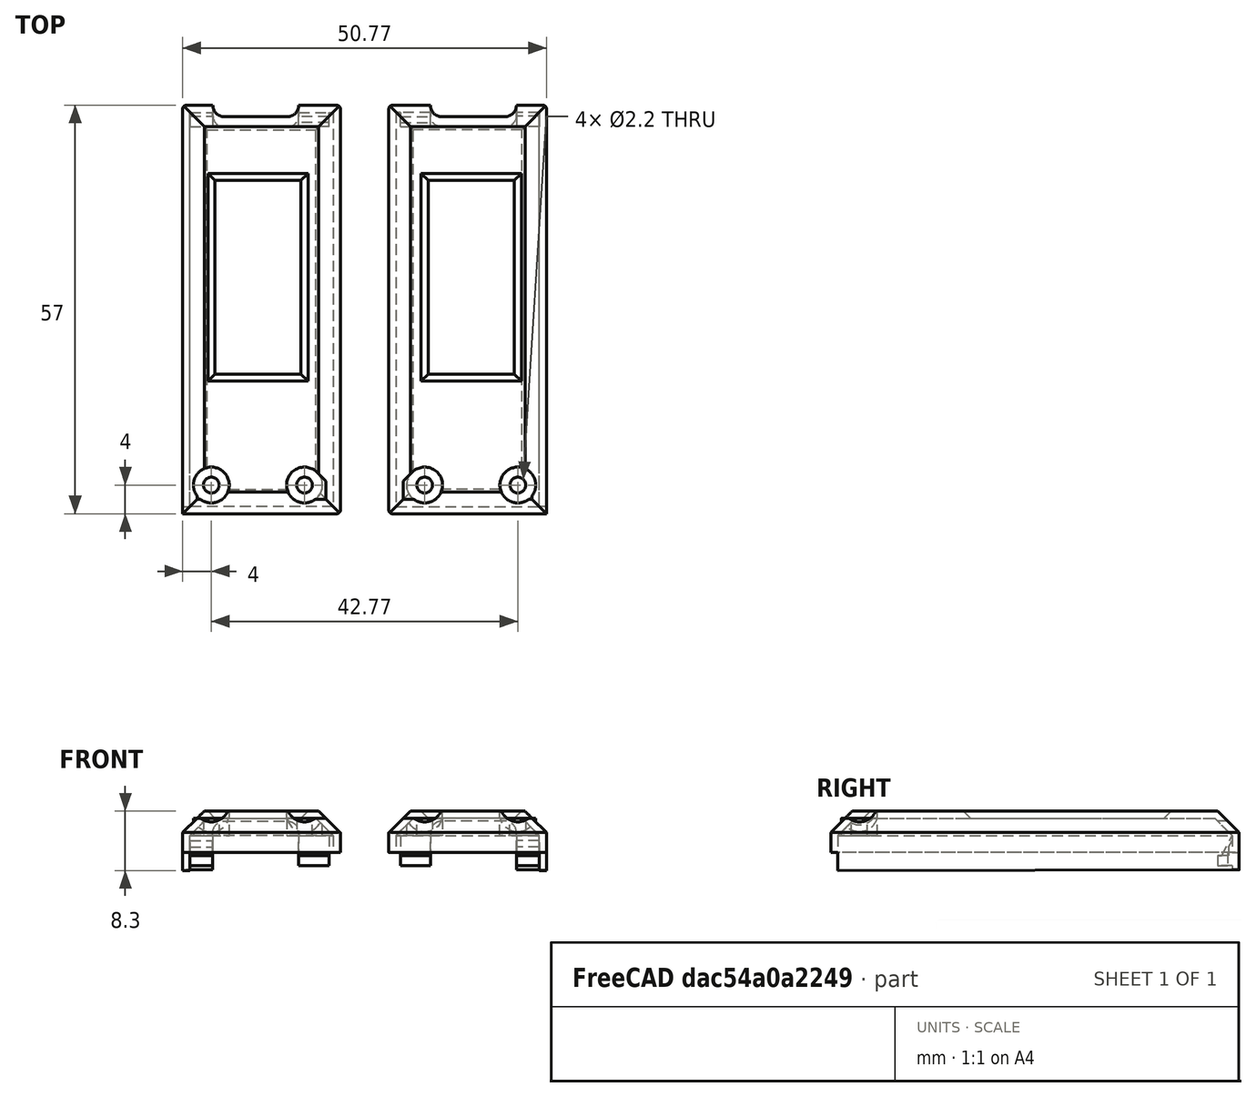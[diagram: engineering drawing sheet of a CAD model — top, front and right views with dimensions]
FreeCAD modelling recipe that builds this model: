
FCSTD DOCUMENT  (FreeCAD 1.0R39285 (Git))
Label: cinque-1.0-cover-Nice
License: All rights reserved
LicenseURL: https://en.wikipedia.org/wiki/All_rights_reserved
objects: Sketcher::SketchObject×13, PartDesign::Pad×6, PartDesign::Pocket×5, PartDesign::Body×2, PartDesign::Chamfer×2, PartDesign::Thickness×1, PartDesign::Fillet×1, Part::Mirroring×1
note: 74 computed .brp shape members not serialized (recipe doc carries the construction recipe); baked Part::Feature solids carry a one-line shape summary decoded from their .brp

FEATURE [PartDesign::Body] Body
  AllowCompound = false
  Origin = -> Origin
FEATURE [Sketcher::SketchObject] Sketch
  ArcFitTolerance = 1e-06
  AttachmentSupport = -> [XY_Plane001]
  FullyConstrained = true
  MakeInternals = false
  MapMode = 5
  sketch-geometry (5):
    g0: LineSegment StartX=-11 StartY=-28.5 StartZ=0 EndX=11 EndY=-28.5 EndZ=0
    g1: LineSegment StartX=11 StartY=-28.5 StartZ=0 EndX=11 EndY=28.5 EndZ=0
    g2: LineSegment StartX=11 StartY=28.5 StartZ=0 EndX=-11 EndY=28.5 EndZ=0
    g3: LineSegment StartX=-11 StartY=28.5 StartZ=0 EndX=-11 EndY=-28.5 EndZ=0
    g4: GeomPoint [constr] X=0 Y=0 Z=0
  constraints (12):
    c: Coincident(g0,g1)
    c: Coincident(g1,g2)
    c: Coincident(g2,g3)
    c: Coincident(g3,g0)
    c: Horizontal(g0)
    c: Horizontal(g2)
    c: Vertical(g1)
    c: Vertical(g3)
    c: Symmetric(g2,g0,g4)
    c: Distance(g1,g3) = 22
    c: Distance(g0,g2) = 57
    c: Coincident(g4,g-1)
FEATURE [PartDesign::Pad] Pad
  Direction = (0,0,1)
  Length = 5.8
  Length2 = 10
  Profile = -> Sketch
  ReferenceAxis = -> Sketch [N_Axis]
  Refine = true
  Suppressed = false
  Type = 0
FEATURE [PartDesign::Chamfer] Chamfer
  Angle = 45
  Base = -> Pad [Face6]
  BaseFeature = -> Pad
  ChamferType = 0
  FlipDirection = false
  Refine = true
  Size = 3
  Size2 = 1
  SupportTransform = false
  Suppressed = false
  UseAllEdges = false
FEATURE [PartDesign::Thickness] Thickness
  Base = -> Chamfer [Face4]
  BaseFeature = -> Chamfer
  Intersection = false
  Join = 0
  Mode = 0
  Refine = true
  Reversed = true
  SupportTransform = false
  Suppressed = false
  Value = 1
FEATURE [Sketcher::SketchObject] Sketch001
  ArcFitTolerance = 1e-06
  AttachmentSupport = -> [Thickness]
  ExternalGeometry = -> [Thickness]
  FullyConstrained = true
  MakeInternals = false
  MapMode = 5
  Placement = pos=(-11,0,0) rot=(0.57735,-0.57735,-0.57735;2.0944rad)
  sketch-geometry (1):
    g0: Circle CenterX=18.5 CenterY=0.2 CenterZ=0 NormalX=0 NormalY=0 NormalZ=1 AngleXU=0 Radius=4.15
  constraints (3):
    c: Diameter(g0) = 8.3
    c: Distance(g0,g-3) = 47
    c: Distance(g0,g-1) = 0.2
FEATURE [Sketcher::SketchObject] Sketch002
  ArcFitTolerance = 1e-06
  AttachmentSupport = -> [Chamfer]
  ExternalGeometry = -> [Chamfer]
  FullyConstrained = true
  MakeInternals = false
  MapMode = 5
  Placement = pos=(0,28.5,0) rot=(0,0.707107,0.707107;3.14159rad)
  sketch-geometry (14):
    g0: LineSegment StartX=-6.8 StartY=-1 StartZ=0 EndX=-6.8 EndY=2.8 EndZ=0
    g1: LineSegment StartX=-5.2 StartY=4.4 StartZ=0 EndX=3.6 EndY=4.4 EndZ=0
    g2: LineSegment StartX=5.2 StartY=2.8 StartZ=0 EndX=5.2 EndY=-1 EndZ=0
    g3: LineSegment StartX=3.6 StartY=-2.6 StartZ=0 EndX=-5.2 EndY=-2.6 EndZ=0
    g4: ArcOfCircle CenterX=-5.2 CenterY=2.8 CenterZ=0 NormalX=0 NormalY=0 NormalZ=1 AngleXU=0 Radius=1.6 StartAngle=1.5708 EndAngle=3.14159
    g5: GeomPoint [constr] X=-6.8 Y=4.4 Z=0
    g6: ArcOfCircle CenterX=3.6 CenterY=2.8 CenterZ=0 NormalX=0 NormalY=0 NormalZ=1 AngleXU=0 Radius=1.6 StartAngle=0 EndAngle=1.5708
    g7: GeomPoint [constr] X=5.2 Y=4.4 Z=0
    g8: ArcOfCircle CenterX=3.6 CenterY=-1 CenterZ=0 NormalX=0 NormalY=0 NormalZ=1 AngleXU=0 Radius=1.6 StartAngle=4.71239 EndAngle=6.28319
    g9: GeomPoint [constr] X=5.2 Y=-2.6 Z=0
    g10: ArcOfCircle CenterX=-5.2 CenterY=-1 CenterZ=0 NormalX=0 NormalY=0 NormalZ=1 AngleXU=0 Radius=1.6 StartAngle=3.14159 EndAngle=4.71239
    g11: GeomPoint [constr] X=-6.8 Y=-2.6 Z=0
    g12: GeomPoint [constr] X=-0.8 Y=4.4 Z=0
    g13: GeomPoint [constr] X=5.2 Y=0.9 Z=0
  constraints (30):
    c: Horizontal(g1)
    c: Parallel(g1,g3)
    c: Parallel(g0,g2)
    c: PointOnObject(g5,g0)
    c: PointOnObject(g5,g1)
    c: Tangent(g0,g4) = 1.5708
    c: Tangent(g1,g4) = 1.5708
    c: PointOnObject(g7,g1)
    c: PointOnObject(g7,g2)
    c: Tangent(g1,g6) = 1.5708
    c: Tangent(g2,g6) = 1.5708
    c: PointOnObject(g9,g2)
    c: PointOnObject(g9,g3)
    c: Tangent(g2,g8) = 1.5708
    c: Tangent(g3,g8) = 1.5708
    c: PointOnObject(g11,g0)
    c: PointOnObject(g11,g3)
    c: Tangent(g0,g10) = 1.5708
    c: Tangent(g3,g10) = 1.5708
    c: Perpendicular(g3,g0)
    c: Symmetric(g1,g1,g12)
    c: Symmetric(g2,g2,g13)
    c: Distance(g13,g-1) = 0.9
    c: Distance(g2,g0) = 12
    c: Distance(g3,g1) = 7
    c: Radius(g10) = 1.6
    c: Radius(g4) = 1.6
    c: Radius(g6) = 1.6
    c: Radius(g8) = 1.6
    c: DistanceX(g12,g-3) = 11.8
FEATURE [PartDesign::Pocket] Pocket001
  BaseFeature = -> Thickness
  Direction = (0,-1,2e-16)
  Length = 5
  Length2 = 5
  Profile = -> Sketch002
  ReferenceAxis = -> Sketch002 [N_Axis]
  Refine = true
  Suppressed = false
  Type = 0
FEATURE [Sketcher::SketchObject] Sketch003
  ArcFitTolerance = 1e-06
  AttachmentOffset = pos=(0,0,4.8) rot=(0,0,1;0rad)
  AttachmentSupport = -> [XY_Plane001]
  ExternalGeometry = -> [Pocket001]
  FullyConstrained = true
  MakeInternals = false
  MapMode = 5
  Placement = pos=(0,0,4.8) rot=(0,0,1;0rad)
  sketch-geometry (3):
    g0: LineSegment [constr] StartX=-11 StartY=-24.5 StartZ=0 EndX=11 EndY=-24.5 EndZ=0
    g1: Circle CenterX=-6 CenterY=-24.5 CenterZ=0 NormalX=0 NormalY=0 NormalZ=1 AngleXU=0 Radius=2.5
    g2: Circle CenterX=7 CenterY=-24.5 CenterZ=0 NormalX=0 NormalY=0 NormalZ=1 AngleXU=0 Radius=2.5
  constraints (10):
    c: PointOnObject(g0,g-4)
    c: Horizontal(g0)
    c: Distance(g0,g-3) = 53
    c: Diameter(g1) = 5
    c: PointOnObject(g1,g0)
    c: Distance(g0,g1) = 5
    c: Diameter(g2) = 5
    c: PointOnObject(g2,g0)
    c: DistanceX(g0,g2) = 18
    c: PointOnObject(g0,g-5)
FEATURE [Sketcher::SketchObject] Sketch004
  ArcFitTolerance = 1e-06
  AttachmentOffset = pos=(0,0,5.8) rot=(0,0,1;0rad)
  AttachmentSupport = -> [XY_Plane001]
  ExternalGeometry = -> [Pocket001]
  FullyConstrained = true
  MakeInternals = false
  MapMode = 5
  Placement = pos=(0,0,5.8) rot=(0,0,1;0rad)
  sketch-geometry (8):
    g0: LineSegment [constr] StartX=-11 StartY=-24.5 StartZ=0 EndX=11 EndY=-24.5 EndZ=0
    g1: ArcOfCircle CenterX=-6 CenterY=-24.5 CenterZ=0 NormalX=0 NormalY=0 NormalZ=1 AngleXU=0 Radius=2.5 StartAngle=4.71239 EndAngle=8.63938
    g2: ArcOfCircle CenterX=7 CenterY=-24.5 CenterZ=0 NormalX=0 NormalY=0 NormalZ=1 AngleXU=0 Radius=2.5 StartAngle=0 EndAngle=4.71239
    g3: LineSegment StartX=-12.0355 StartY=-27 StartZ=0 EndX=-6 EndY=-27 EndZ=0
    g4: LineSegment StartX=9.5 StartY=-24.5 StartZ=0 EndX=9.5 EndY=-27 EndZ=0
    g5: LineSegment StartX=9.5 StartY=-27 StartZ=0 EndX=7 EndY=-27 EndZ=0
    g6: LineSegment StartX=-7.76777 StartY=-22.7322 StartZ=0 EndX=-12.0355 EndY=-27 EndZ=0
    g7: LineSegment [constr] StartX=-6 StartY=-24.5 StartZ=0 EndX=-7.76777 EndY=-22.7322 EndZ=0
  constraints (26):
    c: PointOnObject(g0,g-4)
    c: Horizontal(g0)
    c: Distance(g0,g-3) = 53
    c: Diameter(g1) = 5
    c: PointOnObject(g1,g0)
    c: Distance(g0,g1) = 5
    c: Diameter(g2) = 5
    c: PointOnObject(g2,g0)
    c: DistanceX(g0,g2) = 18
    c: PointOnObject(g0,g-5)
    c: Horizontal(g3)
    c: Vertical(g3,g1)
    c: Coincident(g1,g3)
    c: PointOnObject(g4,g0)
    c: Coincident(g4,g5)
    c: Vertical(g5,g2)
    c: Perpendicular(g4,g5)
    c: Tangent(g4,g2) = 1.5708
    c: Coincident(g2,g5)
    c: PointOnObject(g2,g0)
    c: Coincident(g6,g3)
    c: Angle(g3,g6) = 0.785398
    c: Coincident(g7,g1)
    c: Coincident(g7,g6)
    c: Angle(g0,g7) = 2.35619
    c: Coincident(g1,g6)
FEATURE [Sketcher::SketchObject] Sketch005
  ArcFitTolerance = 1e-06
  AttachmentOffset = pos=(0,0,5.8) rot=(0,0,1;0rad)
  AttachmentSupport = -> [XY_Plane001]
  ExternalGeometry = -> [Pocket001]
  FullyConstrained = true
  MakeInternals = false
  MapMode = 5
  Placement = pos=(0,0,5.8) rot=(0,0,1;0rad)
  sketch-geometry (3):
    g0: LineSegment [constr] StartX=-11 StartY=-24.5 StartZ=0 EndX=11 EndY=-24.5 EndZ=0
    g1: Circle CenterX=-6 CenterY=-24.5 CenterZ=0 NormalX=0 NormalY=0 NormalZ=1 AngleXU=0 Radius=1.1
    g2: Circle CenterX=7 CenterY=-24.5 CenterZ=0 NormalX=0 NormalY=0 NormalZ=1 AngleXU=0 Radius=1.1
  constraints (10):
    c: PointOnObject(g0,g-4)
    c: Horizontal(g0)
    c: Distance(g0,g-3) = 53
    c: Diameter(g1) = 2.2
    c: PointOnObject(g1,g0)
    c: Distance(g0,g1) = 5
    c: Diameter(g2) = 2.2
    c: PointOnObject(g2,g0)
    c: DistanceX(g0,g2) = 18
    c: PointOnObject(g0,g-5)
FEATURE [PartDesign::Pad] Pad001
  BaseFeature = -> Pocket001
  Direction = (0,0,1)
  Length = 2.4
  Length2 = 10
  Profile = -> Sketch003
  ReferenceAxis = -> Sketch003 [N_Axis]
  Refine = true
  Reversed = true
  Suppressed = false
  Type = 0
FEATURE [PartDesign::Pocket] Pocket002
  BaseFeature = -> Pad001
  Direction = (0,0,-1)
  Length = 1
  Length2 = 5
  Profile = -> Sketch004
  ReferenceAxis = -> Sketch004 [N_Axis]
  Refine = true
  Suppressed = false
  Type = 0
FEATURE [PartDesign::Pocket] Pocket003
  BaseFeature = -> Pocket002
  Direction = (0,0,-1)
  Length = 5
  Length2 = 5
  Profile = -> Sketch005
  ReferenceAxis = -> Sketch005 [N_Axis]
  Refine = true
  Suppressed = false
  Type = 0
FEATURE [Sketcher::SketchObject] Sketch006
  ArcFitTolerance = 1e-06
  AttachmentSupport = -> [Pocket003]
  ExternalGeometry = -> [Pocket003]
  FullyConstrained = false
  MakeInternals = false
  MapMode = 5
  Placement = pos=(0,0,5.8) rot=(0,0,1;0rad)
  sketch-geometry (6):
    g0: LineSegment StartX=-5.5 StartY=18 StartZ=0 EndX=-5.5 EndY=-9 EndZ=0
    g1: LineSegment StartX=-5.5 StartY=-9 StartZ=0 EndX=6.5 EndY=-9 EndZ=0
    g2: LineSegment StartX=6.5 StartY=-9 StartZ=0 EndX=6.5 EndY=18 EndZ=0
    g3: LineSegment StartX=6.5 StartY=18 StartZ=0 EndX=-5.5 EndY=18 EndZ=0
    g4: LineSegment [constr] StartX=-6 StartY=-24.5 StartZ=0 EndX=-6 EndY=25.5 EndZ=0
    g5: LineSegment [constr] StartX=7 StartY=-24.5 StartZ=0 EndX=7 EndY=25.5 EndZ=0
  constraints (16):
    c: Coincident(g0,g1)
    c: Coincident(g1,g2)
    c: Coincident(g2,g3)
    c: Coincident(g3,g0)
    c: Vertical(g0)
    c: Vertical(g2)
    c: Horizontal(g1)
    c: Horizontal(g3)
    c: Distance(g0,g-3) = 10.5
    c: DistanceX(g3,g3) = 12
    c: DistanceY(g2,g2) = 27
    c: Distance(g0,g-4) = 5.5
    c: Distance(g4) = 50
    c: Coincident(g4,g-5)
    c: Vertical(g4)
    c: Distance(g5) = 50
FEATURE [Sketcher::SketchObject] Sketch007
  ArcFitTolerance = 1e-06
  AttachmentSupport = -> [Pocket003]
  FullyConstrained = true
  MakeInternals = false
  MapMode = 5
  Placement = pos=(0,0,0) rot=(1,0,0;3.14159rad)
  sketch-geometry (4):
    g0: LineSegment StartX=11 StartY=-28.5 StartZ=0 EndX=11 EndY=-27.5 EndZ=0
    g1: LineSegment StartX=11 StartY=-27.5 StartZ=0 EndX=6.8 EndY=-27.5 EndZ=0
    g2: LineSegment StartX=6.8 StartY=-27.5 StartZ=0 EndX=6.8 EndY=-28.5 EndZ=0
    g3: LineSegment StartX=6.8 StartY=-28.5 StartZ=0 EndX=11 EndY=-28.5 EndZ=0
  constraints (10):
    c: Coincident(g0,g1)
    c: Coincident(g1,g2)
    c: Coincident(g2,g3)
    c: Coincident(g3,g0)
    c: Vertical(g0)
    c: Vertical(g2)
    c: Horizontal(g1)
    c: Distance(g1,g3) = 1
    c: Coincident(g0,g-4)
    c: Coincident(g2,g-4)
FEATURE [PartDesign::Pad] Pad002
  BaseFeature = -> Pocket003
  Direction = (0,0,-1)
  Length = 2.4
  Length2 = 10
  Profile = -> Sketch007
  ReferenceAxis = -> Sketch007 [N_Axis]
  Refine = true
  Suppressed = false
  Type = 0
FEATURE [Sketcher::SketchObject] Sketch008
  ArcFitTolerance = 1e-06
  AttachmentSupport = -> [Pad002]
  ExternalGeometry = -> [Pad002]
  FullyConstrained = true
  MakeInternals = false
  MapMode = 5
  Placement = pos=(10,0,0) rot=(0.57735,-0.57735,-0.57735;2.0944rad)
  sketch-geometry (4):
    g0: LineSegment StartX=27 StartY=0 StartZ=0 EndX=27 EndY=1.2 EndZ=0
    g1: LineSegment StartX=27 StartY=1.2 StartZ=0 EndX=22 EndY=1.4 EndZ=0
    g2: LineSegment StartX=22 StartY=1.4 StartZ=0 EndX=22 EndY=0 EndZ=0
    g3: LineSegment StartX=22 StartY=0 StartZ=0 EndX=27 EndY=0 EndZ=0
  constraints (12):
    c: Vertical(g0)
    c: Coincident(g0,g1)
    c: Coincident(g1,g2)
    c: PointOnObject(g2,g-4)
    c: Vertical(g2)
    c: Coincident(g2,g3)
    c: DistanceY(g0,g-3) = 4.6
    c: DistanceY(g1,g-3) = 4.4
    c: DistanceX(g3,g3) = 5
    c: Coincident(g0,g3)
    c: PointOnObject(g0,g-4)
    c: Distance(g0,g-4) = 0.5
FEATURE [PartDesign::Pocket] Pocket005
  BaseFeature = -> Pad002
  Direction = (1,0,0)
  Length = 19
  Length2 = 5
  Profile = -> Sketch008
  ReferenceAxis = -> Sketch008 [N_Axis]
  Refine = true
  Reversed = true
  Suppressed = false
  Type = 0
FEATURE [Sketcher::SketchObject] Sketch009
  ArcFitTolerance = 1e-06
  AttachmentSupport = -> [Pocket005]
  ExternalGeometry = -> [Pocket005]
  FullyConstrained = true
  MakeInternals = false
  MapMode = 5
  Placement = pos=(11,0,0) rot=(0.57735,0.57735,0.57735;2.0944rad)
  sketch-geometry (4):
    g0: LineSegment StartX=27.5 StartY=0 StartZ=0 EndX=27.5 EndY=-2.4 EndZ=0
    g1: LineSegment StartX=27.5 StartY=-2.4 StartZ=0 EndX=-27.5 EndY=-2.5 EndZ=0
    g2: LineSegment StartX=-27.5 StartY=-2.5 StartZ=0 EndX=-27.5 EndY=0 EndZ=0
    g3: LineSegment StartX=-27.5 StartY=0 StartZ=0 EndX=27.5 EndY=0 EndZ=0
  constraints (9):
    c: Coincident(g0,g1)
    c: Coincident(g1,g2)
    c: Vertical(g2)
    c: Coincident(g2,g3)
    c: Coincident(g3,g0)
    c: Coincident(g2,g-3)
    c: Distance(g2,g2) = 2.5
    c: Coincident(g0,g-4)
    c: Coincident(g0,g-4)
FEATURE [PartDesign::Pad] Pad003
  BaseFeature = -> Pocket005
  Direction = (1,0,0)
  Length = 1
  Length2 = 10
  Profile = -> Sketch009
  ReferenceAxis = -> Sketch009 [N_Axis]
  Refine = true
  Reversed = true
  Suppressed = false
  Type = 0
FEATURE [PartDesign::Fillet] Fillet
  Base = -> Pad003 [Edge76,Edge27,Edge1,Edge5]
  BaseFeature = -> Pad003
  Radius = 0.5
  Refine = true
  SupportTransform = false
  Suppressed = false
  UseAllEdges = false
FEATURE [PartDesign::Pocket] Pocket006
  BaseFeature = -> Fillet
  Direction = (0,0,-1)
  Length = 5
  Length2 = 5
  Profile = -> Sketch006
  ReferenceAxis = -> Sketch006 [N_Axis]
  Refine = true
  Suppressed = false
  Type = 0
FEATURE [PartDesign::Chamfer] Chamfer002
  Angle = 45
  Base = -> Pocket006 [Edge67,Edge66,Edge65,Edge64]
  BaseFeature = -> Pocket006
  ChamferType = 0
  FlipDirection = false
  Refine = true
  Size = 0.99
  Size2 = 1
  SupportTransform = false
  Suppressed = false
  UseAllEdges = false
FEATURE [Sketcher::SketchObject] Sketch010
  ArcFitTolerance = 1e-06
  AttachmentSupport = -> [Chamfer002]
  ExternalGeometry = -> [Chamfer002]
  FullyConstrained = true
  MakeInternals = false
  MapMode = 5
  Placement = pos=(11,0,0) rot=(0.57735,0.57735,0.57735;2.0944rad)
  sketch-geometry (4):
    g0: LineSegment StartX=27.5 StartY=-2.4 StartZ=0 EndX=27.5 EndY=-1.1 EndZ=0
    g1: LineSegment StartX=27.5 StartY=-1.1 StartZ=0 EndX=24.5 EndY=-1.1 EndZ=0
    g2: LineSegment StartX=24.5 StartY=-1.1 StartZ=0 EndX=24.5 EndY=-2.4 EndZ=0
    g3: LineSegment StartX=24.5 StartY=-2.4 StartZ=0 EndX=27.5 EndY=-2.4 EndZ=0
  constraints (11):
    c: Coincident(g0,g1)
    c: Coincident(g1,g2)
    c: Coincident(g2,g3)
    c: Coincident(g3,g0)
    c: Vertical(g0)
    c: Vertical(g2)
    c: Horizontal(g1)
    c: Horizontal(g3)
    c: Distance(g0,g2) = 3
    c: Distance(g1,g3) = 1.3
    c: Coincident(g0,g-4)
FEATURE [Sketcher::SketchObject] Sketch011
  ArcFitTolerance = 1e-06
  AttachmentSupport = -> [Chamfer002]
  ExternalGeometry = -> [Chamfer002]
  FullyConstrained = true
  MakeInternals = false
  MapMode = 5
  Placement = pos=(10,0,0) rot=(0.57735,-0.57735,-0.57735;2.0944rad)
  sketch-geometry (6):
    g0: LineSegment StartX=-27.5 StartY=1.7 StartZ=0 EndX=-27.5 EndY=-1.8 EndZ=0
    g1: LineSegment StartX=-27.5 StartY=-1.8 StartZ=0 EndX=-25.5 EndY=-1.8 EndZ=0
    g2: LineSegment StartX=-27 StartY=0.8 StartZ=0 EndX=-27.5 EndY=1.7 EndZ=0
    g3: LineSegment StartX=-25.5 StartY=-0.4 StartZ=0 EndX=-25.5 EndY=-1.8 EndZ=0
    g4: LineSegment StartX=-27 StartY=0.8 StartZ=0 EndX=-27 EndY=-0.4 EndZ=0
    g5: LineSegment StartX=-27 StartY=-0.4 StartZ=0 EndX=-25.5 EndY=-0.4 EndZ=0
  constraints (18):
    c: PointOnObject(g0,g-3)
    c: Vertical(g0)
    c: Coincident(g0,g1)
    c: Horizontal(g1)
    c: Coincident(g2,g0)
    c: Vertical(g3)
    c: DistanceX(g1,g1) = 2
    c: Coincident(g2,g4)
    c: Vertical(g4)
    c: Coincident(g4,g5)
    c: Coincident(g5,g3)
    c: Horizontal(g5)
    c: Coincident(g1,g3)
    c: DistanceY(g3,g3) = 1.4
    c: Distance(g4,g0) = 0.5
    c: DistanceY(g0,g0) = 3.5
    c: DistanceY(g4,g4) = 1.2
    c: Distance(g3,g-4) = 0.4
FEATURE [PartDesign::Pad] Pad004
  BaseFeature = -> Chamfer002
  Direction = (-1,0,0)
  Length = 3.2
  Length2 = 10
  Profile = -> Sketch011
  ReferenceAxis = -> Sketch011 [N_Axis]
  Refine = true
  Suppressed = false
  Type = 0
FEATURE [Sketcher::SketchObject] Sketch012
  ArcFitTolerance = 1e-06
  AttachmentOffset = pos=(0,0,0.6) rot=(0,0,1;0rad)
  AttachmentSupport = -> [Pad004]
  ExternalGeometry = -> [Pad004]
  FullyConstrained = true
  MakeInternals = false
  MapMode = 5
  Placement = pos=(-9.4,0,0) rot=(0.57735,0.57735,0.57735;2.0944rad)
  sketch-geometry (7):
    g0: LineSegment StartX=27.5 StartY=2.38579 StartZ=0 EndX=27.5 EndY=0 EndZ=0
    g1: LineSegment StartX=25.5 StartY=-1.8 StartZ=0 EndX=26.9 EndY=-1.8 EndZ=0
    g2: LineSegment StartX=27.5 StartY=0 StartZ=0 EndX=26.9 EndY=0 EndZ=0
    g3: LineSegment StartX=26.9 StartY=0 StartZ=0 EndX=26.9 EndY=-1.8 EndZ=0
    g4: LineSegment StartX=25.5 StartY=-1.8 StartZ=0 EndX=25.5 EndY=-0.4 EndZ=0
    g5: LineSegment StartX=25.5 StartY=-0.4 StartZ=0 EndX=26.1 EndY=-0.4 EndZ=0
    g6: LineSegment StartX=26.1 StartY=-0.4 StartZ=0 EndX=27.5 EndY=2.38579 EndZ=0
  constraints (20):
    c: PointOnObject(g0,g-1)
    c: Vertical(g0)
    c: Horizontal(g1)
    c: Coincident(g0,g2)
    c: PointOnObject(g2,g-1)
    c: Coincident(g2,g3)
    c: Coincident(g3,g1)
    c: Coincident(g1,g4)
    c: Vertical(g4)
    c: Coincident(g4,g5)
    c: Horizontal(g5)
    c: Coincident(g5,g6)
    c: DistanceX(g2,g2) = 0.6
    c: Distance(g1,g0) = 2
    c: Distance(g-1,g5) = 0.4
    c: DistanceY(g4,g4) = 1.4
    c: Coincident(g6,g0)
    c: Coincident(g-3,g0)
    c: DistanceX(g5,g2) = 0.8
    c: Vertical(g3)
FEATURE [PartDesign::Pad] Pad005
  BaseFeature = -> Pad004
  Direction = (1,0,0)
  Length = 4.2
  Length2 = 10
  Profile = -> Sketch012
  ReferenceAxis = -> Sketch012 [N_Axis]
  Refine = true
  Suppressed = false
  Type = 0
FEATURE [PartDesign::Body] Body001
  AllowCompound = false
  Group = -> [Sketch,Pad,Chamfer,Thickness,Sketch001,Sketch002,Pocket001,Sketch003,Sketch004,Sketch005,Pad001,Pocket002,Pocket003,Sketch006,Sketch007,Pad002,Sketch008,Pocket005,Sketch009,Pad003,Fillet,Pocket006,Chamfer002,Sketch010,Sketch011,Pad004,Sketch012,Pad005]
  Origin = -> Origin001
  Tip = -> Pad005
FEATURE [Part::Mirroring] Part__Mirroring  label="Pad005 (Mirror #1)"
  Base = (0,0,0)
  Normal = (1,0,0)
  Placement = pos=(-28.77,0,0) rot=(0,0,1;0rad)
  Source = -> Pad005
